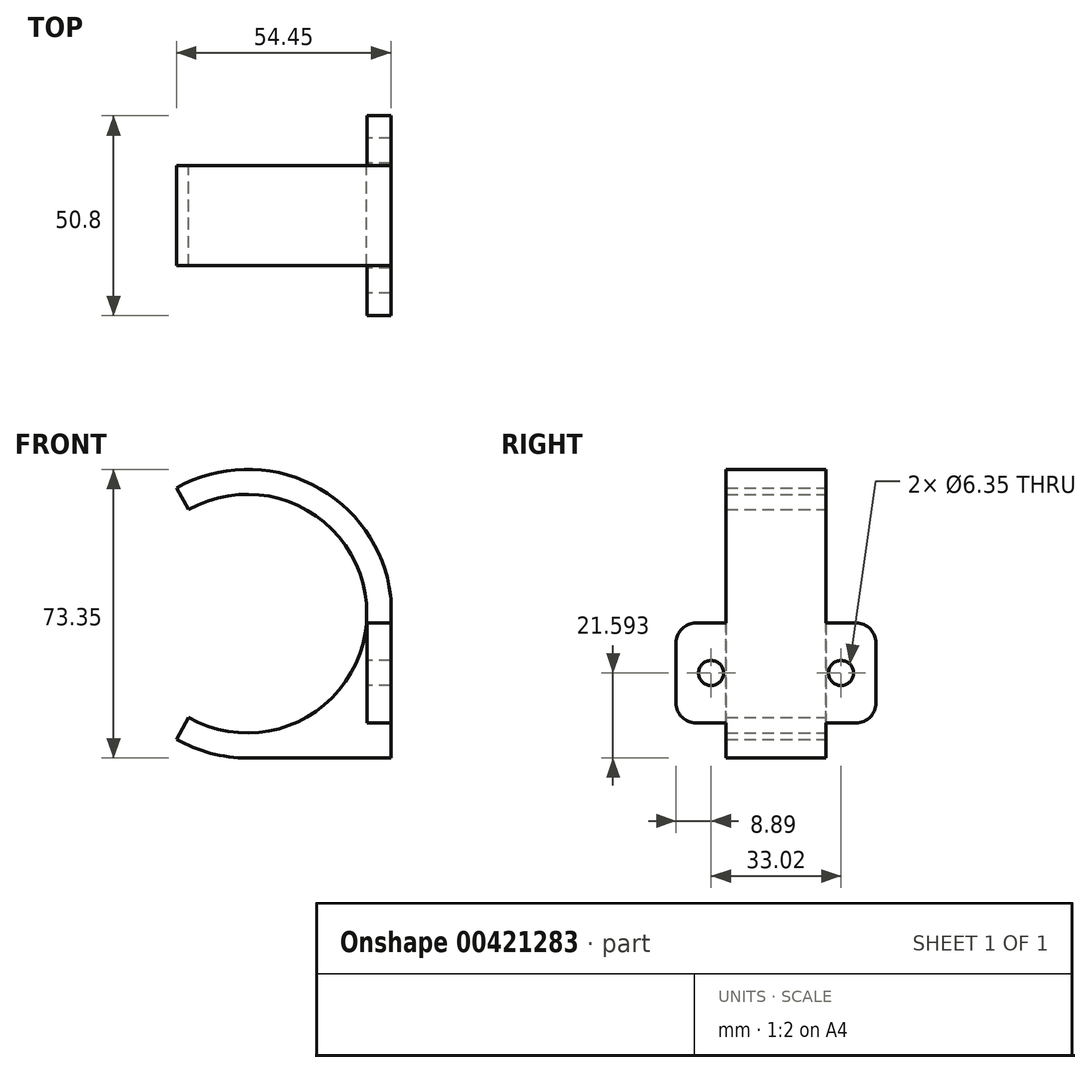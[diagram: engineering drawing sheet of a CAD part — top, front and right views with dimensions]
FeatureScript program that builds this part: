
annotation { "Feature Type Name" : "Feature", "Feature Type Description" : "" }
export const myFeature = defineFeature(function(context is Context, id is Id, definition is map)
    precondition{}
    {
        {
            var Q0;
            Q0=qCreatedBy(makeId("Top.planeOp"),FACE);
            cPlane(context, id + "F0", {"entities" : qUnion([Q0]), "cplaneType" : CPlaneType.OFFSET, "offset" : 30.35 * mm, "width" : 152.4 * mm, "height" : 152.4 * mm});
        }
        {
            var Q0;
            Q0=qCreatedBy(makeId("Front.planeOp"),FACE);
            var sketch = newSketch(context, id + "F1", { "sketchPlane" : qUnion([Q0])});
            skPoint(sketch, "E0.visualSharp", {"position": v(0, 0) * mm});
            skArc(sketch, "E1", {"start": v(-45.21, 29.76) * mm, "mid": v(-4.19, 58.44) * mm, "end": v(-45.79, 86.3) * mm});
            skPoint(sketch, "E2.visualSharp", {"position": v(-9.8, 92.84) * mm});
            skArc(sketch, "E3", {"start": v(-45.79, 86.3) * mm, "mid": v(-47.63, 85.48) * mm, "end": v(-49.41, 84.55) * mm});
            skArc(sketch, "E4.trimOffspring", {"start": v(-49.41, 31.72) * mm, "mid": v(-47.35, 30.66) * mm, "end": v(-45.21, 29.76) * mm});
            skArc(sketch, "E5.0", {"start": v(-48.15, 92.19) * mm, "mid": v(-50.37, 91.2) * mm, "end": v(-52.53, 90.08) * mm});
            skArc(sketch, "E5.1", {"start": v(-47.45, 23.81) * mm, "mid": v(-41.1, 22.05) * mm, "end": v(-34.52, 21.46) * mm});
            skArc(sketch, "E5.2", {"start": v(-52.53, 26.19) * mm, "mid": v(-50.04, 24.9) * mm, "end": v(-47.45, 23.81) * mm});
            skLineSegment(sketch, "E6", {"start": v(-52.53, 90.08) * mm, "end": v(-49.41, 84.55) * mm});
            skLineSegment(sketch, "E7", {"start": v(-49.41, 31.72) * mm, "end": v(-52.53, 26.19) * mm});
            skLineSegment(sketch, "E8", {"start": v(-34.52, 21.46) * mm, "end": v(1.92, 21.46) * mm});
            skLineSegment(sketch, "E9", {"start": v(1.92, 21.46) * mm, "end": v(1.92, 62.37) * mm});
            skArc(sketch, "E10.trimOffspring", {"start": v(-34.52, 94.81) * mm, "mid": v(-41.46, 94.15) * mm, "end": v(-48.15, 92.19) * mm});
            skLineSegment(sketch, "E11", {"start": v(-4.19, 58.13) * mm, "end": v(-4.19, 58.13) * mm});
            skPoint(sketch, "E11.startSnap0", {"position": v(-4.19, 58.44) * mm});
            skPoint(sketch, "E11.endSnap0", {"position": v(-4.19, 58.44) * mm});
            skArc(sketch, "E12.trimOffspring", {"start": v(1.92, 62.37) * mm, "mid": v(-15.75, 89.65) * mm, "end": v(-48.15, 92.19) * mm});
            skPoint(sketch, "E13.orphan", {"position": v(1.92, 94.81) * mm});
            skPoint(sketch, "E14.orphan", {"position": v(1.92, 58.44) * mm});
            skSolve(sketch);
        }
        {
            var Q0;
            Q0 = qSketchRegion(id + "F1", true);
            extrude(context, id + "F2", {"entities" : qUnion([Q0]), "depth" : 25.4 * mm, "offsetDistance" : 25.4 * mm});
        }
        {
            var Q0;
            Q0=qCreatedBy(id+"F0.planeOp",FACE);
            var sketch = newSketch(context, id + "F3", { "sketchPlane" : qUnion([Q0])});
            skLineSegment(sketch, "E15", {"start": v(1.92, 12.7) * mm, "end": v(1.92, -38.1) * mm});
            skLineSegment(sketch, "E16", {"start": v(1.92, -38.1) * mm, "end": v(-4.18, -38.1) * mm});
            skLineSegment(sketch, "E17", {"start": v(-4.18, -38.1) * mm, "end": v(-4.18, 12.7) * mm});
            skLineSegment(sketch, "E18", {"start": v(-4.18, 12.7) * mm, "end": v(1.92, 12.7) * mm});
            skSolve(sketch);
        }
        {
            var Q0;
            Q0 = qSketchRegion(id + "F3", true);
            extrude(context, id + "F4", {"entities" : qUnion([Q0]), "operationType" : NewBodyOperationType.ADD, "depth" : 25.4 * mm, "offsetDistance" : 25.4 * mm});
        }
        {
            var Q0;
            Q0=makeQuery(id+"F2.opExtrude","SWEPT_EDGE",EDGE,{"disambiguationData":[OSD([sQuery(id+"F1.wireOp",EDGE,"E9"),sQuery(id+"F1.wireOp",EDGE,"E12.trimOffspring")])]});
            var Q1;
            Q1=makeQuery(id+"F4.opExtrude","CAP_EDGE",EDGE,{"disambiguationData":[OSD([sQuery(id+"F3.wireOp",EDGE,"878a14ae-7fa2-416b-9d30-1deaf584c23a0.MirrorCS")])],"isStart":false});
            var Q2;
            Q2=makeQuery(id+"F4.opExtrude","CAP_EDGE",EDGE,{"disambiguationData":[OSD([sQuery(id+"F3.wireOp",EDGE,"878a14ae-7fa2-416b-9d30-1deaf584c23a0.MirrorCS")])],"isStart":true});
            var Q3;
            Q3=makeQuery(id+"F4.opExtrude","CAP_EDGE",EDGE,{"disambiguationData":[OSD([sQuery(id+"F3.wireOp",EDGE,"EcTSXGU2-ivze-5ZqL-1PV5-1DGGiddeig6I")])],"isStart":true});
            var Q4;
            Q4=makeQuery(id+"F4.opExtrude","CAP_EDGE",EDGE,{"disambiguationData":[OSD([sQuery(id+"F3.wireOp",EDGE,"EcTSXGU2-ivze-5ZqL-1PV5-1DGGiddeig6I")])],"isStart":false});
            var Q5;
            Q5=makeQuery(id+"F4.opExtrude","CAP_EDGE",EDGE,{"disambiguationData":[OSD([sQuery(id+"F3.wireOp",EDGE,"41060de9-5cb8-49ae-ae4b-f649ff0304df0.MirrorCS")])],"isStart":false});
            var Q6;
            Q6=makeQuery(id+"F4.opExtrude","CAP_EDGE",EDGE,{"disambiguationData":[OSD([sQuery(id+"F3.wireOp",EDGE,"41060de9-5cb8-49ae-ae4b-f649ff0304df0.MirrorCS")])],"isStart":true});
            var Q7;
            Q7=makeQuery(id+"F4.opExtrude","CAP_EDGE",EDGE,{"disambiguationData":[OSD([sQuery(id+"F3.wireOp",EDGE,"E16")])],"isStart":false});
            var Q8;
            Q8=makeQuery(id+"F4.opExtrude","CAP_EDGE",EDGE,{"disambiguationData":[OSD([sQuery(id+"F3.wireOp",EDGE,"E16")])],"isStart":true});
            var Q9;
            Q9=makeQuery(id+"F4.opExtrude","CAP_EDGE",EDGE,{"disambiguationData":[OSD([sQuery(id+"F3.wireOp",EDGE,"E18")])],"isStart":true});
            var Q10;
            Q10=makeQuery(id+"F4.opExtrude","CAP_EDGE",EDGE,{"disambiguationData":[OSD([sQuery(id+"F3.wireOp",EDGE,"E18")])],"isStart":false});
            fillet(context, id + "F5", {"entities" : qUnion([Q0, Q1, Q2, Q3, Q4, Q5, Q6, Q7, Q8, Q9, Q10]), "radius" : 5.08 * mm, "tangentPropagation" : true, "allowEdgeOverflow" : false});
        }
        {
            var Q0;
            {var subQ0=sQuery(id+"F3.wireOp",EDGE,"E18");var subQ1=sQuery(id+"F3.wireOp",EDGE,"E17");Q0=makeQuery(id+"F4.boolean.opBoolean","SPLIT",FACE,{"disambiguationData":[TD([makeQuery(id+"F4.opExtrude","SWEPT_FACE",FACE,{"disambiguationData":[OSD([subQ0])]})])],"derivedFrom":makeQuery(id+"F4.opExtrude","SWEPT_FACE",FACE,{"disambiguationData":[OSD([subQ1])]})});}
            var sketch = newSketch(context, id + "F6", { "sketchPlane" : qUnion([Q0])});
            skPoint(sketch, "E19", {"position": v(-3.8, 43.05) * mm});
            skCircle(sketch, "E20", {"center": v(-3.8, 43.05) * mm, "radius": 3.18 * mm});
            skLineSegment(sketch, "E21", {"start": v(-3.8, 43.05) * mm, "end": v(-10.16, 43.05) * mm, "construction": true});
            skLineSegment(sketch, "E22", {"start": v(-3.8, 43.05) * mm, "end": v(-3.8, 30.35) * mm, "construction": true});
            skSolve(sketch);
        }
        {
            var Q0;
            Q0 = qSketchRegion(id + "F6", true);
            extrude(context, id + "F7", {"entities" : qUnion([Q0]), "operationType" : NewBodyOperationType.REMOVE, "endBound" : BoundingType.THROUGH_ALL, "oppositeDirection" : true, "depth" : 25.4 * mm, "offsetDistance" : 25.4 * mm});
        }
        {
            var Q0;
            {var subQ1=sQuery(id+"F3.wireOp",EDGE,"E17");var subQ2=sQuery(id+"F3.wireOp",EDGE,"E16");Q0=makeQuery(id+"F4.boolean.opBoolean","SPLIT",FACE,{"disambiguationData":[TD([makeQuery(id+"F4.opExtrude","SWEPT_FACE",FACE,{"disambiguationData":[OSD([subQ2])]})])],"derivedFrom":makeQuery(id+"F4.opExtrude","SWEPT_FACE",FACE,{"disambiguationData":[OSD([subQ1])]})});}
            var sketch = newSketch(context, id + "F8", { "sketchPlane" : qUnion([Q0])});
            skPoint(sketch, "E23", {"position": v(29.2, 43.05) * mm});
            skCircle(sketch, "E24", {"center": v(29.2, 43.05) * mm, "radius": 3.18 * mm});
            skLineSegment(sketch, "E25", {"start": v(35.56, 43.05) * mm, "end": v(29.2, 43.05) * mm, "construction": true});
            skLineSegment(sketch, "E26", {"start": v(29.2, 43.05) * mm, "end": v(29.21, 30.35) * mm, "construction": true});
            skSolve(sketch);
        }
        {
            var Q0;
            Q0 = qSketchRegion(id + "F8", true);
            extrude(context, id + "F9", {"entities" : qUnion([Q0]), "operationType" : NewBodyOperationType.REMOVE, "endBound" : BoundingType.THROUGH_ALL, "oppositeDirection" : true, "depth" : 25.4 * mm, "offsetDistance" : 25.4 * mm});
        }
    });
